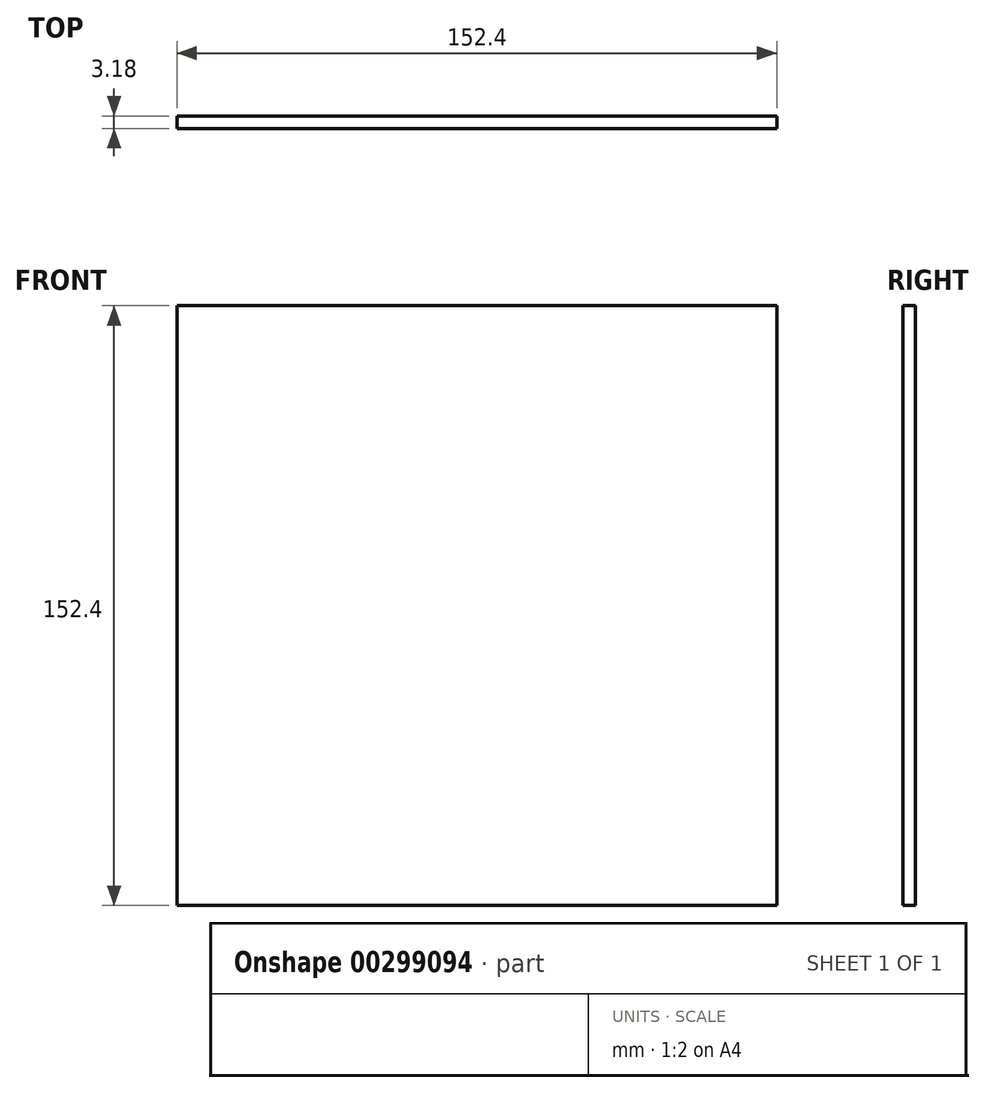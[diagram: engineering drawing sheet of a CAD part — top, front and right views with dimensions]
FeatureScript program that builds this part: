
annotation { "Feature Type Name" : "Feature", "Feature Type Description" : "" }
export const myFeature = defineFeature(function(context is Context, id is Id, definition is map)
    precondition{}
    {
        {
            var Q0;
            Q0=qCreatedBy(makeId("Front.planeOp"),FACE);
            var sketch = newSketch(context, id + "F0", { "sketchPlane" : qUnion([Q0])});
            skLineSegment(sketch, "E0.bottom", {"start": v(-76.2, 76.2) * mm, "end": v(76.2, 76.2) * mm});
            skLineSegment(sketch, "E0.top", {"start": v(-76.2, -76.2) * mm, "end": v(76.2, -76.2) * mm});
            skLineSegment(sketch, "E0.left", {"start": v(-76.2, 76.2) * mm, "end": v(-76.2, -76.2) * mm});
            skLineSegment(sketch, "E0.right", {"start": v(76.2, 76.2) * mm, "end": v(76.2, -76.2) * mm});
            skPoint(sketch, "E0.middle", {"position": v(0, 0) * mm});
            skSolve(sketch);
        }
        {
            var Q0;
            Q0=makeQuery(id+"F0.imprint","IMPRINT",FACE,{"disambiguationData":[TD([[makeQuery(id+"F0.imprint","IMPRINT",EDGE,{"derivedFrom":sQuery(id+"F0.wireOp",EDGE,"E0.bottom")}),-1.0]])]});
            extrude(context, id + "F1", {"entities" : qUnion([Q0]), "endBound" : BoundingType.SYMMETRIC, "depth" : 3.17 * mm});
        }
    });
